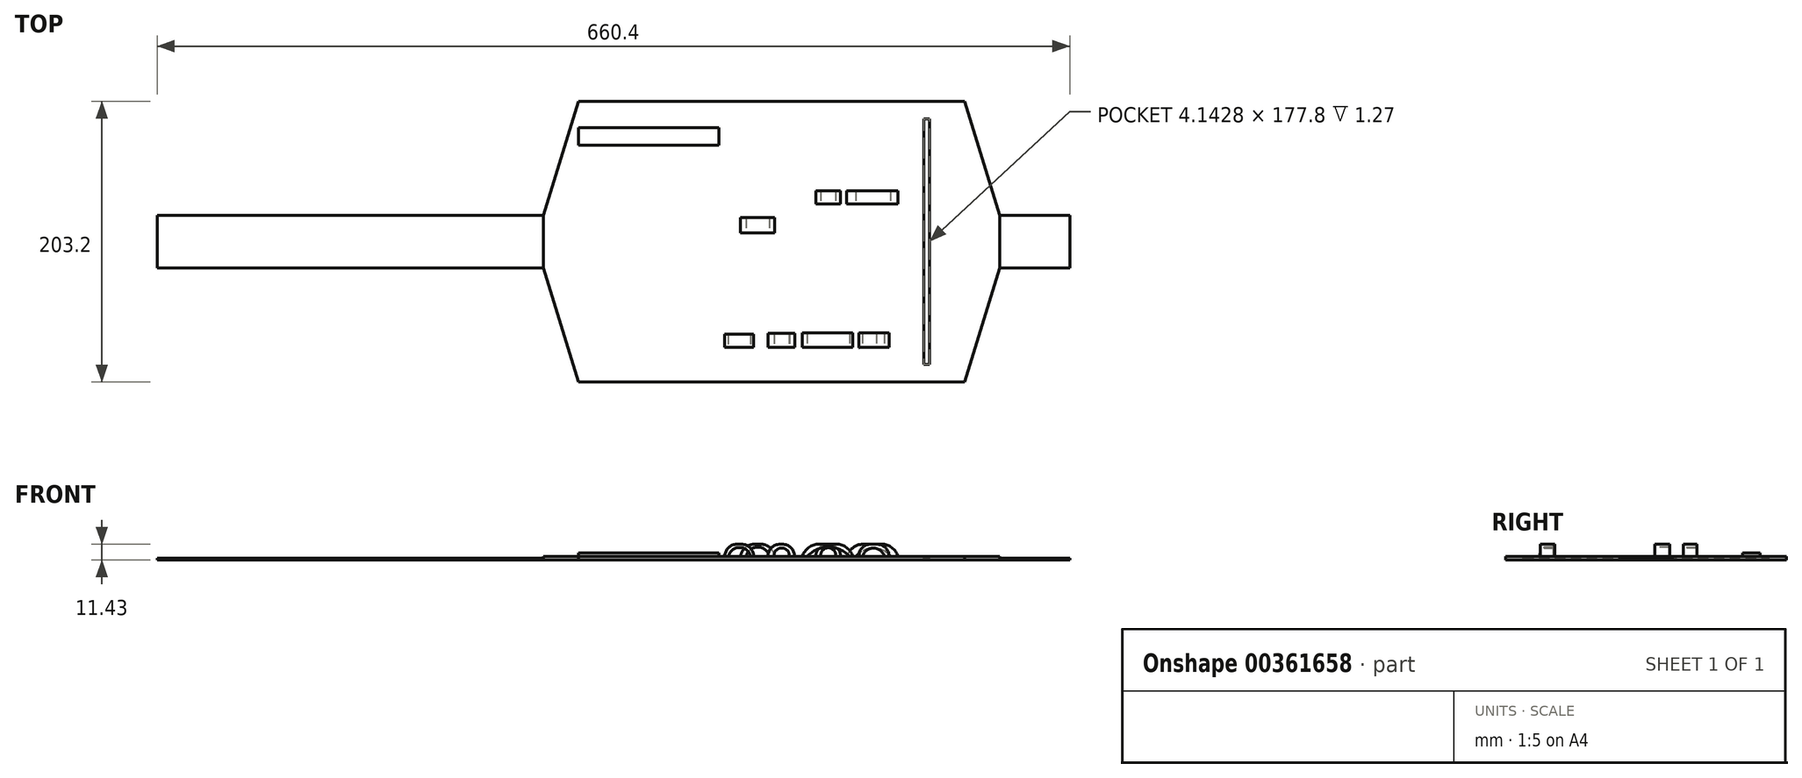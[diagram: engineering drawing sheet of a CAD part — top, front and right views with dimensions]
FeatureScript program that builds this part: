
annotation { "Feature Type Name" : "Feature", "Feature Type Description" : "" }
export const myFeature = defineFeature(function(context is Context, id is Id, definition is map)
    precondition{}
    {
        {
            var Q0;
            Q0=qCreatedBy(makeId("Top.planeOp"),FACE);
            var sketch = newSketch(context, id + "F0", { "sketchPlane" : qUnion([Q0])});
            skLineSegment(sketch, "E0.bottom", {"start": v(0, 0) * mm, "end": v(-304.8, 0) * mm});
            skLineSegment(sketch, "E0.top", {"start": v(0, 38.1) * mm, "end": v(-304.8, 38.1) * mm});
            skLineSegment(sketch, "E0.left", {"start": v(0, 0) * mm, "end": v(0, 38.1) * mm});
            skLineSegment(sketch, "E0.right", {"start": v(-304.8, 0) * mm, "end": v(-304.8, 38.1) * mm});
            skLineSegment(sketch, "E1", {"start": v(0, 38.1) * mm, "end": v(-25.4, 38.1) * mm});
            skLineSegment(sketch, "E2.bottom", {"start": v(-25.4, 38.1) * mm, "end": v(0, 38.1) * mm});
            skLineSegment(sketch, "E2.top", {"start": v(-25.4, 0) * mm, "end": v(0, 0) * mm});
            skLineSegment(sketch, "E2.left", {"start": v(-25.4, 38.1) * mm, "end": v(-25.4, 0) * mm});
            skLineSegment(sketch, "E2.right", {"start": v(0, 38.1) * mm, "end": v(0, 0) * mm});
            skSolve(sketch);
        }
        {
            var Q0;
            Q0=makeQuery(id+"F0.imprint","IMPRINT",FACE,{"disambiguationData":[TD([[makeQuery(id+"F0.imprint","IMPRINT",EDGE,{"derivedFrom":sQuery(id+"F0.wireOp",EDGE,"E0.bottom")}),-1.0]])]});
            extrude(context, id + "F1", {"entities" : qUnion([Q0]), "depth" : 1.27 * mm});
        }
        {
            var Q0;
            Q0=qCreatedBy(makeId("Top.planeOp"),FACE);
            var sketch = newSketch(context, id + "F2", { "sketchPlane" : qUnion([Q0])});
            skLineSegment(sketch, "E3.left", {"start": v(0, 0) * mm, "end": v(0, 38.1) * mm});
            skLineSegment(sketch, "E3.right", {"start": v(-25.4, 0) * mm, "end": v(-25.4, 38.1) * mm});
            skLineSegment(sketch, "E4", {"start": v(0, 120.65) * mm, "end": v(0, 38.1) * mm});
            skLineSegment(sketch, "E5", {"start": v(-25.4, 38.1) * mm, "end": v(0, 120.65) * mm});
            skLineSegment(sketch, "E6", {"start": v(0, 0) * mm, "end": v(0, -82.55) * mm});
            skLineSegment(sketch, "E7", {"start": v(-25.4, 0) * mm, "end": v(0, -82.55) * mm});
            skLineSegment(sketch, "E8.bottom", {"start": v(0, 120.65) * mm, "end": v(279.4, 120.65) * mm});
            skLineSegment(sketch, "E8.top", {"start": v(0, -82.55) * mm, "end": v(279.4, -82.55) * mm});
            skLineSegment(sketch, "E8.left", {"start": v(0, 120.65) * mm, "end": v(0, -82.55) * mm});
            skLineSegment(sketch, "E8.right", {"start": v(279.4, 120.65) * mm, "end": v(279.4, -82.55) * mm});
            skLineSegment(sketch, "E9", {"start": v(304.8, 0) * mm, "end": v(304.8, 38.1) * mm});
            skLineSegment(sketch, "E10", {"start": v(279.4, 120.65) * mm, "end": v(304.8, 38.1) * mm});
            skLineSegment(sketch, "E11", {"start": v(279.4, -82.55) * mm, "end": v(304.8, 0) * mm});
            skLineSegment(sketch, "E12", {"start": v(101.6, -63.5) * mm, "end": v(0, -63.5) * mm});
            skLineSegment(sketch, "E13", {"start": v(101.6, 101.6) * mm, "end": v(0, 101.6) * mm});
            skLineSegment(sketch, "E14", {"start": v(0, 101.6) * mm, "end": v(0, -63.5) * mm});
            skLineSegment(sketch, "E15", {"start": v(101.6, 101.6) * mm, "end": v(101.6, -63.5) * mm});
            skSolve(sketch);
        }
        {
            var Q0;
            Q0=makeQuery(id+"F2.imprint","IMPRINT",FACE,{"disambiguationData":[TD([[makeQuery(id+"F2.imprint","IMPRINT",EDGE,{"derivedFrom":sQuery(id+"F2.wireOp",EDGE,"E3.right")}),-1.0]])]});
            var Q1;
            {var subQ4=sQuery(id+"F2.wireOp",EDGE,"E8.bottom");Q1=makeQuery(id+"F2.imprint","IMPRINT",FACE,{"disambiguationData":[TD([[makeQuery(id+"F2.imprint","IMPRINT",EDGE,{"derivedFrom":subQ4}),-1.0]])]});}
            var Q2;
            Q2=makeQuery(id+"F2.imprint","IMPRINT",FACE,{"disambiguationData":[TD([[makeQuery(id+"F2.imprint","IMPRINT",EDGE,{"derivedFrom":sQuery(id+"F2.wireOp",EDGE,"E8.right")}),1.0]])]});
            extrude(context, id + "F3", {"entities" : qUnion([Q0, Q1, Q2]), "operationType" : NewBodyOperationType.ADD, "depth" : 2.54 * mm});
        }
        {
            var Q0;
            Q0=makeQuery(id+"F3.opExtrude","CAP_FACE",FACE,{"disambiguationData":[OSD([sQuery(id+"F2.wireOp",EDGE,"E3.right"),sQuery(id+"F2.wireOp",EDGE,"E5"),sQuery(id+"F2.wireOp",EDGE,"E7"),sQuery(id+"F2.wireOp",EDGE,"E8.bottom"),sQuery(id+"F2.wireOp",EDGE,"E8.top"),sQuery(id+"F2.wireOp",EDGE,"E9"),sQuery(id+"F2.wireOp",EDGE,"E10"),sQuery(id+"F2.wireOp",EDGE,"E11"),sQuery(id+"F2.wireOp",EDGE,"E12"),sQuery(id+"F2.wireOp",EDGE,"E13"),sQuery(id+"F2.wireOp",EDGE,"E14"),sQuery(id+"F2.wireOp",EDGE,"E15")])],"isStart":false});
            var sketch = newSketch(context, id + "F4", { "sketchPlane" : qUnion([Q0])});
            skLineSegment(sketch, "E16", {"start": v(0, -63.5) * mm, "end": v(101.6, -63.5) * mm});
            skLineSegment(sketch, "E17", {"start": v(101.6, -63.5) * mm, "end": v(101.6, 101.6) * mm});
            skLineSegment(sketch, "E18", {"start": v(101.6, 101.6) * mm, "end": v(0, 101.6) * mm});
            skLineSegment(sketch, "E19", {"start": v(0, 101.6) * mm, "end": v(0, -63.5) * mm});
            skSolve(sketch);
        }
        {
            var Q0;
            Q0=makeQuery(id+"F4.imprint","IMPRINT",FACE,{"disambiguationData":[TD([[makeQuery(id+"F4.imprint","IMPRINT",EDGE,{"derivedFrom":sQuery(id+"F4.wireOp",EDGE,"E16")}),-1.0]])]});
            extrude(context, id + "F5", {"entities" : qUnion([Q0]), "oppositeDirection" : true, "depth" : 2.54 * mm});
        }
        {
            var Q0;
            Q0=makeQuery(id+"F3.opExtrude","CAP_FACE",FACE,{"disambiguationData":[OSD([sQuery(id+"F2.wireOp",EDGE,"E3.right"),sQuery(id+"F2.wireOp",EDGE,"E5"),sQuery(id+"F2.wireOp",EDGE,"E7"),sQuery(id+"F2.wireOp",EDGE,"E8.bottom"),sQuery(id+"F2.wireOp",EDGE,"E8.top"),sQuery(id+"F2.wireOp",EDGE,"E9"),sQuery(id+"F2.wireOp",EDGE,"E10"),sQuery(id+"F2.wireOp",EDGE,"E11"),sQuery(id+"F2.wireOp",EDGE,"E12"),sQuery(id+"F2.wireOp",EDGE,"E13"),sQuery(id+"F2.wireOp",EDGE,"E14"),sQuery(id+"F2.wireOp",EDGE,"E15")])],"isStart":false});
            var sketch = newSketch(context, id + "F6", { "sketchPlane" : qUnion([Q0])});
            skLineSegment(sketch, "E20.bottom", {"start": v(0, 101.6) * mm, "end": v(101.6, 101.6) * mm});
            skLineSegment(sketch, "E20.top", {"start": v(0, 88.9) * mm, "end": v(101.6, 88.9) * mm});
            skLineSegment(sketch, "E20.left", {"start": v(0, 101.6) * mm, "end": v(0, 88.9) * mm});
            skLineSegment(sketch, "E20.right", {"start": v(101.6, 101.6) * mm, "end": v(101.6, 88.9) * mm});
            skSolve(sketch);
        }
        {
            var Q0;
            Q0 = qSketchRegion(id + "F6", true);
            extrude(context, id + "F7", {"entities" : qUnion([Q0]), "operationType" : NewBodyOperationType.ADD, "depth" : 2.54 * mm});
        }
        {
            var Q0;
            Q0=makeQuery(id+"F3.opExtrude","CAP_FACE",FACE,{"disambiguationData":[OSD([sQuery(id+"F2.wireOp",EDGE,"E3.right"),sQuery(id+"F2.wireOp",EDGE,"E5"),sQuery(id+"F2.wireOp",EDGE,"E7"),sQuery(id+"F2.wireOp",EDGE,"E8.bottom"),sQuery(id+"F2.wireOp",EDGE,"E8.top"),sQuery(id+"F2.wireOp",EDGE,"E9"),sQuery(id+"F2.wireOp",EDGE,"E10"),sQuery(id+"F2.wireOp",EDGE,"E11"),sQuery(id+"F2.wireOp",EDGE,"E12"),sQuery(id+"F2.wireOp",EDGE,"E13"),sQuery(id+"F2.wireOp",EDGE,"E14"),sQuery(id+"F2.wireOp",EDGE,"E15")])],"isStart":false});
            var sketch = newSketch(context, id + "F8", { "sketchPlane" : qUnion([Q0])});
            skLineSegment(sketch, "E21", {"start": v(304.8, 38.1) * mm, "end": v(304.8, 0) * mm});
            skLineSegment(sketch, "E22", {"start": v(304.8, 0) * mm, "end": v(355.6, 0) * mm});
            skLineSegment(sketch, "E23.bottom", {"start": v(355.6, 0) * mm, "end": v(304.8, 0) * mm});
            skLineSegment(sketch, "E23.top", {"start": v(355.6, 38.1) * mm, "end": v(304.8, 38.1) * mm});
            skLineSegment(sketch, "E23.left", {"start": v(355.6, 0) * mm, "end": v(355.6, 38.1) * mm});
            skLineSegment(sketch, "E23.right", {"start": v(304.8, 0) * mm, "end": v(304.8, 38.1) * mm});
            skSolve(sketch);
        }
        {
            var Q0;
            Q0 = qSketchRegion(id + "F8", true);
            extrude(context, id + "F9", {"entities" : qUnion([Q0]), "operationType" : NewBodyOperationType.ADD, "oppositeDirection" : true, "depth" : 2.54 * mm});
        }
        {
            var Q0;
            Q0=makeQuery(id+"F9.boolean.opBoolean","MERGE",FACE,{"derivedFrom":[makeQuery(id+"F3.opExtrude","CAP_FACE",FACE,{"disambiguationData":[OSD([sQuery(id+"F2.wireOp",EDGE,"E3.right"),sQuery(id+"F2.wireOp",EDGE,"E5"),sQuery(id+"F2.wireOp",EDGE,"E7"),sQuery(id+"F2.wireOp",EDGE,"E8.bottom"),sQuery(id+"F2.wireOp",EDGE,"E8.top"),sQuery(id+"F2.wireOp",EDGE,"E9"),sQuery(id+"F2.wireOp",EDGE,"E10"),sQuery(id+"F2.wireOp",EDGE,"E11"),sQuery(id+"F2.wireOp",EDGE,"E12"),sQuery(id+"F2.wireOp",EDGE,"E13"),sQuery(id+"F2.wireOp",EDGE,"E14"),sQuery(id+"F2.wireOp",EDGE,"E15")])],"isStart":false}),makeQuery(id+"F9.opExtrude","CAP_FACE",FACE,{"disambiguationData":[OSD([sQuery(id+"F8.wireOp",EDGE,"E23.bottom"),sQuery(id+"F8.wireOp",EDGE,"E23.top"),sQuery(id+"F8.wireOp",EDGE,"E23.left"),sQuery(id+"F8.wireOp",EDGE,"E23.right")])],"isStart":true})]});
            var sketch = newSketch(context, id + "F10", { "sketchPlane" : qUnion([Q0])});
            skLineSegment(sketch, "E24.bottom", {"start": v(355.6, 38.1) * mm, "end": v(304.8, 38.1) * mm});
            skLineSegment(sketch, "E24.top", {"start": v(355.6, 0) * mm, "end": v(304.8, 0) * mm});
            skLineSegment(sketch, "E24.left", {"start": v(355.6, 38.1) * mm, "end": v(355.6, 0) * mm});
            skLineSegment(sketch, "E24.right", {"start": v(304.8, 38.1) * mm, "end": v(304.8, 0) * mm});
            skSolve(sketch);
        }
        {
            var Q0;
            Q0 = qSketchRegion(id + "F10", true);
            extrude(context, id + "F11", {"entities" : qUnion([Q0]), "operationType" : NewBodyOperationType.REMOVE, "oppositeDirection" : true, "depth" : 1.27 * mm});
        }
        {
            var Q0;
            Q0=makeQuery(id+"F9.boolean.opBoolean","MERGE",FACE,{"derivedFrom":[makeQuery(id+"F3.opExtrude","CAP_FACE",FACE,{"disambiguationData":[OSD([sQuery(id+"F2.wireOp",EDGE,"E3.right"),sQuery(id+"F2.wireOp",EDGE,"E5"),sQuery(id+"F2.wireOp",EDGE,"E7"),sQuery(id+"F2.wireOp",EDGE,"E8.bottom"),sQuery(id+"F2.wireOp",EDGE,"E8.top"),sQuery(id+"F2.wireOp",EDGE,"E9"),sQuery(id+"F2.wireOp",EDGE,"E10"),sQuery(id+"F2.wireOp",EDGE,"E11"),sQuery(id+"F2.wireOp",EDGE,"E12"),sQuery(id+"F2.wireOp",EDGE,"E13"),sQuery(id+"F2.wireOp",EDGE,"E14"),sQuery(id+"F2.wireOp",EDGE,"E15")])],"isStart":false}),makeQuery(id+"F9.opExtrude","CAP_FACE",FACE,{"disambiguationData":[OSD([sQuery(id+"F8.wireOp",EDGE,"E23.bottom"),sQuery(id+"F8.wireOp",EDGE,"E23.top"),sQuery(id+"F8.wireOp",EDGE,"E23.left"),sQuery(id+"F8.wireOp",EDGE,"E23.right")])],"isStart":true})]});
            var sketch = newSketch(context, id + "F12", { "sketchPlane" : qUnion([Q0])});
            skLineSegment(sketch, "E25.bottom", {"start": v(254, -69.85) * mm, "end": v(249.86, -69.85) * mm});
            skLineSegment(sketch, "E25.top", {"start": v(254, 107.95) * mm, "end": v(249.86, 107.95) * mm});
            skLineSegment(sketch, "E25.left", {"start": v(254, -69.85) * mm, "end": v(254, 107.95) * mm});
            skLineSegment(sketch, "E25.right", {"start": v(249.86, -69.85) * mm, "end": v(249.86, 107.95) * mm});
            skSolve(sketch);
        }
        {
            var Q0;
            Q0 = qSketchRegion(id + "F12", true);
            extrude(context, id + "F13", {"entities" : qUnion([Q0]), "operationType" : NewBodyOperationType.REMOVE, "oppositeDirection" : true, "depth" : 1.27 * mm});
        }
        {
            var Q0;
            Q0=makeQuery(id+"F9.boolean.opBoolean","MERGE",FACE,{"derivedFrom":[makeQuery(id+"F3.opExtrude","CAP_FACE",FACE,{"disambiguationData":[OSD([sQuery(id+"F2.wireOp",EDGE,"E3.right"),sQuery(id+"F2.wireOp",EDGE,"E5"),sQuery(id+"F2.wireOp",EDGE,"E7"),sQuery(id+"F2.wireOp",EDGE,"E8.bottom"),sQuery(id+"F2.wireOp",EDGE,"E8.top"),sQuery(id+"F2.wireOp",EDGE,"E9"),sQuery(id+"F2.wireOp",EDGE,"E10"),sQuery(id+"F2.wireOp",EDGE,"E11"),sQuery(id+"F2.wireOp",EDGE,"E12"),sQuery(id+"F2.wireOp",EDGE,"E13"),sQuery(id+"F2.wireOp",EDGE,"E14"),sQuery(id+"F2.wireOp",EDGE,"E15")])],"isStart":false}),makeQuery(id+"F9.opExtrude","CAP_FACE",FACE,{"disambiguationData":[OSD([sQuery(id+"F8.wireOp",EDGE,"E23.bottom"),sQuery(id+"F8.wireOp",EDGE,"E23.top"),sQuery(id+"F8.wireOp",EDGE,"E23.left"),sQuery(id+"F8.wireOp",EDGE,"E23.right")])],"isStart":true})]});
            var sketch = newSketch(context, id + "F14", { "sketchPlane" : qUnion([Q0])});
            skSolve(sketch);
        }
        {
            var Q0;
            Q0=makeQuery(id+"F14.imprint","IMPRINT",FACE,{"disambiguationData":[TD([[makeQuery(id+"F14.imprint","IMPRINT",EDGE,{"derivedFrom":makeQuery(id+"F3.opExtrude","CAP_EDGE",EDGE,{"disambiguationData":[OSD([sQuery(id+"F2.wireOp",EDGE,"E3.right")])],"isStart":false})}),-1.0]])]});
            var sketch = newSketch(context, id + "F15", { "sketchPlane" : qUnion([Q0])});
            skLineSegment(sketch, "E26.bottom", {"start": v(105.97, -47.87) * mm, "end": v(126.9, -47.87) * mm});
            skLineSegment(sketch, "E26.top", {"start": v(105.97, -57.4) * mm, "end": v(126.9, -57.4) * mm});
            skLineSegment(sketch, "E26.left", {"start": v(105.97, -47.87) * mm, "end": v(105.97, -57.4) * mm});
            skLineSegment(sketch, "E26.right", {"start": v(126.9, -47.87) * mm, "end": v(126.9, -57.4) * mm});
            skLineSegment(sketch, "E27.bottom", {"start": v(137.17, -47.45) * mm, "end": v(156.52, -47.45) * mm});
            skLineSegment(sketch, "E27.top", {"start": v(137.17, -57.4) * mm, "end": v(156.52, -57.4) * mm});
            skLineSegment(sketch, "E27.left", {"start": v(137.17, -47.45) * mm, "end": v(137.17, -57.4) * mm});
            skLineSegment(sketch, "E27.right", {"start": v(156.52, -47.45) * mm, "end": v(156.52, -57.4) * mm});
            skLineSegment(sketch, "E28.bottom", {"start": v(117.44, 36.33) * mm, "end": v(142.06, 36.33) * mm});
            skLineSegment(sketch, "E28.top", {"start": v(117.44, 25.28) * mm, "end": v(142.06, 25.28) * mm});
            skLineSegment(sketch, "E28.left", {"start": v(117.44, 36.33) * mm, "end": v(117.44, 25.28) * mm});
            skLineSegment(sketch, "E28.right", {"start": v(142.06, 36.33) * mm, "end": v(142.06, 25.28) * mm});
            skLineSegment(sketch, "E29.bottom", {"start": v(162.06, -47.03) * mm, "end": v(198.7, -47.03) * mm});
            skLineSegment(sketch, "E29.top", {"start": v(162.06, -57.4) * mm, "end": v(198.7, -57.4) * mm});
            skLineSegment(sketch, "E29.left", {"start": v(162.06, -47.03) * mm, "end": v(162.06, -57.4) * mm});
            skLineSegment(sketch, "E29.right", {"start": v(198.7, -47.03) * mm, "end": v(198.7, -57.4) * mm});
            skLineSegment(sketch, "E30.bottom", {"start": v(171.8, 55.9) * mm, "end": v(189.76, 55.9) * mm});
            skLineSegment(sketch, "E30.top", {"start": v(171.8, 46.21) * mm, "end": v(189.76, 46.21) * mm});
            skLineSegment(sketch, "E30.left", {"start": v(171.8, 55.9) * mm, "end": v(171.8, 46.21) * mm});
            skLineSegment(sketch, "E30.right", {"start": v(189.76, 55.9) * mm, "end": v(189.76, 46.21) * mm});
            skLineSegment(sketch, "E31.bottom", {"start": v(194.26, 55.97) * mm, "end": v(231.44, 55.97) * mm});
            skLineSegment(sketch, "E31.top", {"start": v(194.26, 46.21) * mm, "end": v(231.44, 46.21) * mm});
            skLineSegment(sketch, "E31.left", {"start": v(194.26, 55.97) * mm, "end": v(194.26, 46.21) * mm});
            skLineSegment(sketch, "E31.right", {"start": v(231.44, 55.97) * mm, "end": v(231.44, 46.21) * mm});
            skLineSegment(sketch, "E32.bottom", {"start": v(202.9, -47.03) * mm, "end": v(224.87, -47.03) * mm});
            skLineSegment(sketch, "E32.top", {"start": v(202.9, -57.89) * mm, "end": v(224.87, -57.89) * mm});
            skLineSegment(sketch, "E32.left", {"start": v(202.9, -47.03) * mm, "end": v(202.9, -57.89) * mm});
            skLineSegment(sketch, "E32.right", {"start": v(224.87, -47.03) * mm, "end": v(224.87, -57.89) * mm});
            skSolve(sketch);
        }
        {
            var Q0;
            Q0 = qSketchRegion(id + "F15", true);
            extrude(context, id + "F16", {"entities" : qUnion([Q0]), "operationType" : NewBodyOperationType.ADD, "depth" : 8.9 * mm});
        }
        {
            var Q0;
            Q0=makeQuery(id+"F16.opExtrude","CAP_EDGE",EDGE,{"disambiguationData":[OSD([sQuery(id+"F15.wireOp",EDGE,"E26.left")])],"isStart":false});
            var Q1;
            Q1=makeQuery(id+"F16.opExtrude","CAP_EDGE",EDGE,{"disambiguationData":[OSD([sQuery(id+"F15.wireOp",EDGE,"E26.right")])],"isStart":false});
            var Q2;
            Q2=makeQuery(id+"F16.opExtrude","CAP_EDGE",EDGE,{"disambiguationData":[OSD([sQuery(id+"F15.wireOp",EDGE,"E27.left")])],"isStart":false});
            var Q3;
            Q3=makeQuery(id+"F16.opExtrude","CAP_EDGE",EDGE,{"disambiguationData":[OSD([sQuery(id+"F15.wireOp",EDGE,"E27.right")])],"isStart":false});
            var Q4;
            Q4=makeQuery(id+"F16.opExtrude","CAP_EDGE",EDGE,{"disambiguationData":[OSD([sQuery(id+"F15.wireOp",EDGE,"E32.left")])],"isStart":false});
            var Q5;
            Q5=makeQuery(id+"F16.opExtrude","CAP_EDGE",EDGE,{"disambiguationData":[OSD([sQuery(id+"F15.wireOp",EDGE,"E32.right")])],"isStart":false});
            var Q6;
            Q6=makeQuery(id+"F16.opExtrude","CAP_EDGE",EDGE,{"disambiguationData":[OSD([sQuery(id+"F15.wireOp",EDGE,"E30.right")])],"isStart":false});
            var Q7;
            Q7=makeQuery(id+"F16.opExtrude","CAP_EDGE",EDGE,{"disambiguationData":[OSD([sQuery(id+"F15.wireOp",EDGE,"E30.left")])],"isStart":false});
            fillet(context, id + "F17", {"entities" : qUnion([Q0, Q1, Q2, Q3, Q4, Q5, Q6, Q7]), "radius" : 8.9 * mm, "tangentPropagation" : true, "allowEdgeOverflow" : false});
        }
        {
            var Q0;
            Q0=makeQuery(id+"F16.opExtrude","CAP_EDGE",EDGE,{"disambiguationData":[OSD([sQuery(id+"F15.wireOp",EDGE,"E28.left")])],"isStart":false});
            var Q1;
            Q1=makeQuery(id+"F16.opExtrude","CAP_EDGE",EDGE,{"disambiguationData":[OSD([sQuery(id+"F15.wireOp",EDGE,"E28.right")])],"isStart":false});
            fillet(context, id + "F18", {"entities" : qUnion([Q0, Q1]), "radius" : 10.16 * mm, "tangentPropagation" : true, "allowEdgeOverflow" : false});
        }
        {
            var Q0;
            Q0=makeQuery(id+"F16.opExtrude","CAP_EDGE",EDGE,{"disambiguationData":[OSD([sQuery(id+"F15.wireOp",EDGE,"E29.left")])],"isStart":false});
            var Q1;
            Q1=makeQuery(id+"F16.opExtrude","CAP_EDGE",EDGE,{"disambiguationData":[OSD([sQuery(id+"F15.wireOp",EDGE,"E29.right")])],"isStart":false});
            var Q2;
            Q2=makeQuery(id+"F16.opExtrude","CAP_EDGE",EDGE,{"disambiguationData":[OSD([sQuery(id+"F15.wireOp",EDGE,"E31.left")])],"isStart":false});
            var Q3;
            Q3=makeQuery(id+"F16.opExtrude","CAP_EDGE",EDGE,{"disambiguationData":[OSD([sQuery(id+"F15.wireOp",EDGE,"E31.right")])],"isStart":false});
            fillet(context, id + "F19", {"entities" : qUnion([Q0, Q1, Q2, Q3]), "radius" : 12.7 * mm, "tangentPropagation" : true, "allowEdgeOverflow" : false});
        }
        {
            var Q0;
            Q0=makeQuery(id+"F16.opExtrude","SWEPT_FACE",FACE,{"disambiguationData":[OSD([sQuery(id+"F15.wireOp",EDGE,"E28.top")])]});
            var sketch = newSketch(context, id + "F20", { "sketchPlane" : qUnion([Q0])});
            skArc(sketch, "E33", {"start": v(138.3, 2.54) * mm, "mid": v(129.85, 9.3) * mm, "end": v(121.4, 2.54) * mm});
            skLineSegment(sketch, "E34", {"start": v(121.4, 2.54) * mm, "end": v(138.3, 2.54) * mm});
            skSolve(sketch);
        }
        {
            var Q0;
            Q0 = qSketchRegion(id + "F20", true);
            extrude(context, id + "F21", {"entities" : qUnion([Q0]), "operationType" : NewBodyOperationType.REMOVE, "oppositeDirection" : true, "depth" : 25.4 * mm});
        }
        {
            var Q0;
            Q0=makeQuery(id+"F16.opExtrude","SWEPT_FACE",FACE,{"disambiguationData":[OSD([sQuery(id+"F15.wireOp",EDGE,"E30.top")])]});
            var sketch = newSketch(context, id + "F22", { "sketchPlane" : qUnion([Q0])});
            skArc(sketch, "E35", {"start": v(186.26, 2.54) * mm, "mid": v(180.85, 8.77) * mm, "end": v(175.43, 2.54) * mm});
            skArc(sketch, "E36", {"start": v(226.03, 2.54) * mm, "mid": v(213.5, 8.61) * mm, "end": v(200.95, 2.54) * mm});
            skLineSegment(sketch, "E37", {"start": v(175.43, 2.54) * mm, "end": v(186.26, 2.54) * mm});
            skLineSegment(sketch, "E38", {"start": v(200.95, 2.54) * mm, "end": v(226.03, 2.54) * mm});
            skSolve(sketch);
        }
        {
            var Q0;
            Q0 = qSketchRegion(id + "F22", true);
            extrude(context, id + "F23", {"entities" : qUnion([Q0]), "operationType" : NewBodyOperationType.REMOVE, "oppositeDirection" : true, "depth" : 25.4 * mm});
        }
        {
            var Q0;
            Q0=makeQuery(id+"F16.opExtrude","SWEPT_FACE",FACE,{"disambiguationData":[OSD([sQuery(id+"F15.wireOp",EDGE,"E26.top")])]});
            var sketch = newSketch(context, id + "F24", { "sketchPlane" : qUnion([Q0])});
            skArc(sketch, "E39", {"start": v(124.76, 2.54) * mm, "mid": v(116.67, 9.03) * mm, "end": v(108.58, 2.54) * mm});
            skPoint(sketch, "E39.endSnap0", {"position": v(108.58, 8.83) * mm});
            skArc(sketch, "E40", {"start": v(152.69, 2.54) * mm, "mid": v(147.15, 8.7) * mm, "end": v(141.62, 2.54) * mm});
            skArc(sketch, "E41", {"start": v(196.26, 2.54) * mm, "mid": v(180.98, 9.32) * mm, "end": v(165.69, 2.54) * mm});
            skArc(sketch, "E42", {"start": v(221.55, 2.54) * mm, "mid": v(214.03, 8.53) * mm, "end": v(206.52, 2.54) * mm});
            skLineSegment(sketch, "E43", {"start": v(108.58, 2.54) * mm, "end": v(124.76, 2.54) * mm});
            skLineSegment(sketch, "E44", {"start": v(141.62, 2.54) * mm, "end": v(152.69, 2.54) * mm});
            skLineSegment(sketch, "E45", {"start": v(165.69, 2.54) * mm, "end": v(196.26, 2.54) * mm});
            skLineSegment(sketch, "E46", {"start": v(206.52, 2.54) * mm, "end": v(221.55, 2.54) * mm});
            skSolve(sketch);
        }
        {
            var Q0;
            Q0 = qSketchRegion(id + "F24", true);
            extrude(context, id + "F25", {"entities" : qUnion([Q0]), "operationType" : NewBodyOperationType.REMOVE, "oppositeDirection" : true, "depth" : 25.4 * mm});
        }
        {
            var Q0;
            Q0=makeQuery(id+"F16.opExtrude","CAP_FACE",FACE,{"disambiguationData":[OSD([sQuery(id+"F15.wireOp",EDGE,"E32.bottom"),sQuery(id+"F15.wireOp",EDGE,"E32.top"),sQuery(id+"F15.wireOp",EDGE,"E32.left"),sQuery(id+"F15.wireOp",EDGE,"E32.right")])],"isStart":false});
            var sketch = newSketch(context, id + "F26", { "sketchPlane" : qUnion([Q0])});
            skLineSegment(sketch, "E47.bottom", {"start": v(203.22, -57.48) * mm, "end": v(225.14, -57.48) * mm});
            skLineSegment(sketch, "E47.top", {"start": v(203.22, -57.89) * mm, "end": v(225.14, -57.89) * mm});
            skLineSegment(sketch, "E47.left", {"start": v(203.22, -57.48) * mm, "end": v(203.22, -57.89) * mm});
            skLineSegment(sketch, "E47.right", {"start": v(225.14, -57.48) * mm, "end": v(225.14, -57.89) * mm});
            skSolve(sketch);
        }
        {
            var Q0;
            Q0 = qSketchRegion(id + "F26", true);
            extrude(context, id + "F27", {"entities" : qUnion([Q0]), "operationType" : NewBodyOperationType.REMOVE, "oppositeDirection" : true, "depth" : 8.9 * mm});
        }
        {
            var Q0;
            Q0=makeQuery(id+"F27.boolean.opBoolean","COPY",FACE,{"derivedFrom":makeQuery(id+"F27.opExtrude","SWEPT_FACE",FACE,{"disambiguationData":[OSD([sQuery(id+"F26.wireOp",EDGE,"E47.bottom")])]})});
            var sketch = newSketch(context, id + "F28", { "sketchPlane" : qUnion([Q0])});
            skArc(sketch, "E48", {"start": v(221.43, 2.54) * mm, "mid": v(213.57, 8.63) * mm, "end": v(205.71, 2.54) * mm});
            skLineSegment(sketch, "E49", {"start": v(205.71, 2.54) * mm, "end": v(221.43, 2.54) * mm});
            skSolve(sketch);
        }
        {
            var Q0;
            Q0=makeQuery(id+"F28.imprint","IMPRINT",FACE,{"disambiguationData":[TD([[makeQuery(id+"F28.imprint","IMPRINT",EDGE,{"derivedFrom":sQuery(id+"F28.wireOp",EDGE,"E48")}),1.0]])]});
            extrude(context, id + "F29", {"entities" : qUnion([Q0]), "operationType" : NewBodyOperationType.REMOVE, "oppositeDirection" : true, "depth" : 25.4 * mm});
        }
    });
